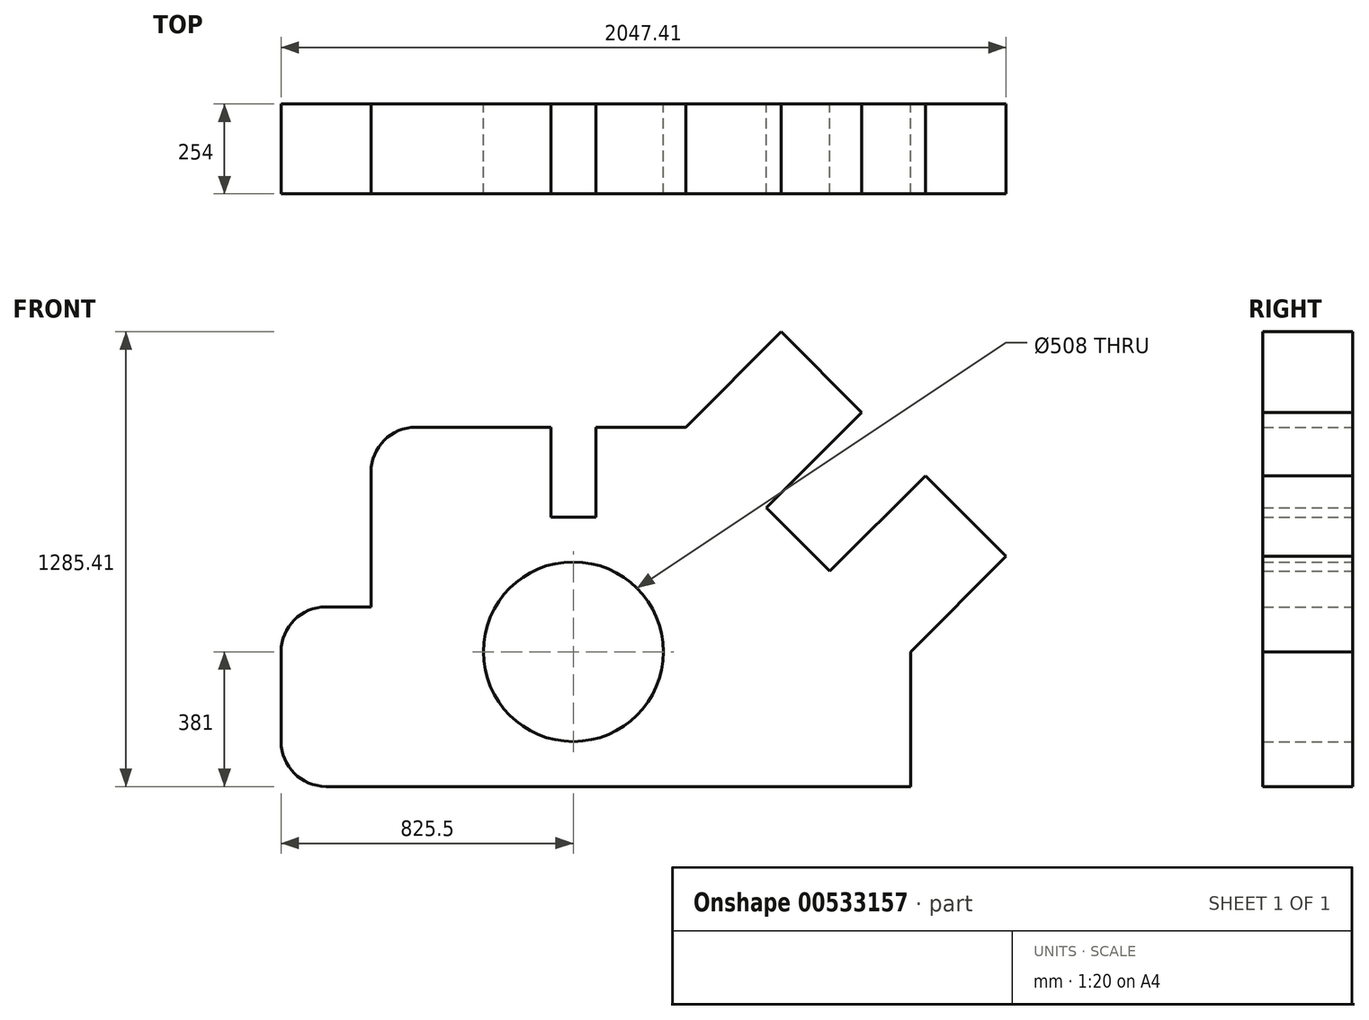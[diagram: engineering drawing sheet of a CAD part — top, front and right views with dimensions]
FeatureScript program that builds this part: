
annotation { "Feature Type Name" : "Feature", "Feature Type Description" : "" }
export const myFeature = defineFeature(function(context is Context, id is Id, definition is map)
    precondition{}
    {
        {
            var Q0;
            Q0=qCreatedBy(makeId("Front.planeOp"),FACE);
            var sketch = newSketch(context, id + "F0", { "sketchPlane" : qUnion([Q0])});
            skLineSegment(sketch, "E0", {"start": v(127, 0) * mm, "end": v(1778, 0) * mm});
            skLineSegment(sketch, "E1", {"start": v(1778, 0) * mm, "end": v(1778, 381) * mm});
            skLineSegment(sketch, "E2", {"start": v(0, 127) * mm, "end": v(0, 381) * mm});
            skLineSegment(sketch, "E3", {"start": v(127, 508) * mm, "end": v(254, 508) * mm});
            skLineSegment(sketch, "E4", {"start": v(254, 508) * mm, "end": v(254, 889) * mm});
            skLineSegment(sketch, "E5", {"start": v(381, 1016) * mm, "end": v(762, 1016) * mm});
            skLineSegment(sketch, "E6", {"start": v(762, 1016) * mm, "end": v(762, 762) * mm});
            skLineSegment(sketch, "E7", {"start": v(762, 762) * mm, "end": v(889, 762) * mm});
            skLineSegment(sketch, "E8", {"start": v(889, 762) * mm, "end": v(889, 1016) * mm});
            skLineSegment(sketch, "E9", {"start": v(889, 1016) * mm, "end": v(1143, 1016) * mm});
            skLineSegment(sketch, "E10", {"start": v(1778, 381) * mm, "end": v(2047.4, 650.4) * mm});
            skLineSegment(sketch, "E11", {"start": v(2047.4, 650.4) * mm, "end": v(1819.71, 878.1) * mm});
            skLineSegment(sketch, "E12", {"start": v(1819.71, 878.1) * mm, "end": v(1550.3, 608.7) * mm});
            skLineSegment(sketch, "E13", {"start": v(1550.3, 608.7) * mm, "end": v(1370.7, 788.3) * mm});
            skLineSegment(sketch, "E14", {"start": v(1370.7, 788.3) * mm, "end": v(1640.1, 1057.71) * mm});
            skLineSegment(sketch, "E15", {"start": v(1640.1, 1057.71) * mm, "end": v(1412.4, 1285.4) * mm});
            skLineSegment(sketch, "E16", {"start": v(1412.4, 1285.4) * mm, "end": v(1143, 1016) * mm});
            skPoint(sketch, "E17.visualSharp", {"position": v(254, 1016) * mm});
            skArc(sketch, "E17.filletArc", {"start": v(381, 1016) * mm, "mid": v(291.2, 978.8) * mm, "end": v(254, 889) * mm});
            skPoint(sketch, "E18.visualSharp", {"position": v(0, 508) * mm});
            skArc(sketch, "E18.filletArc", {"start": v(127, 508) * mm, "mid": v(37.2, 470.8) * mm, "end": v(0, 381) * mm});
            skPoint(sketch, "E19.visualSharp", {"position": v(0, 0) * mm});
            skArc(sketch, "E19.filletArc", {"start": v(0, 127) * mm, "mid": v(37.2, 37.2) * mm, "end": v(127, 0) * mm});
            skCircle(sketch, "E20", {"center": v(825.5, 381) * mm, "radius": 254 * mm});
            skSolve(sketch);
        }
        {
            var Q0;
            Q0=makeQuery(id+"F0.imprint","IMPRINT",FACE,{"disambiguationData":[TD([[makeQuery(id+"F0.imprint","IMPRINT",EDGE,{"derivedFrom":sQuery(id+"F0.wireOp",EDGE,"E0")}),1.0]])]});
            extrude(context, id + "F1", {"entities" : qUnion([Q0]), "depth" : 254 * mm, "offsetDistance" : 25.4 * mm});
        }
    });
